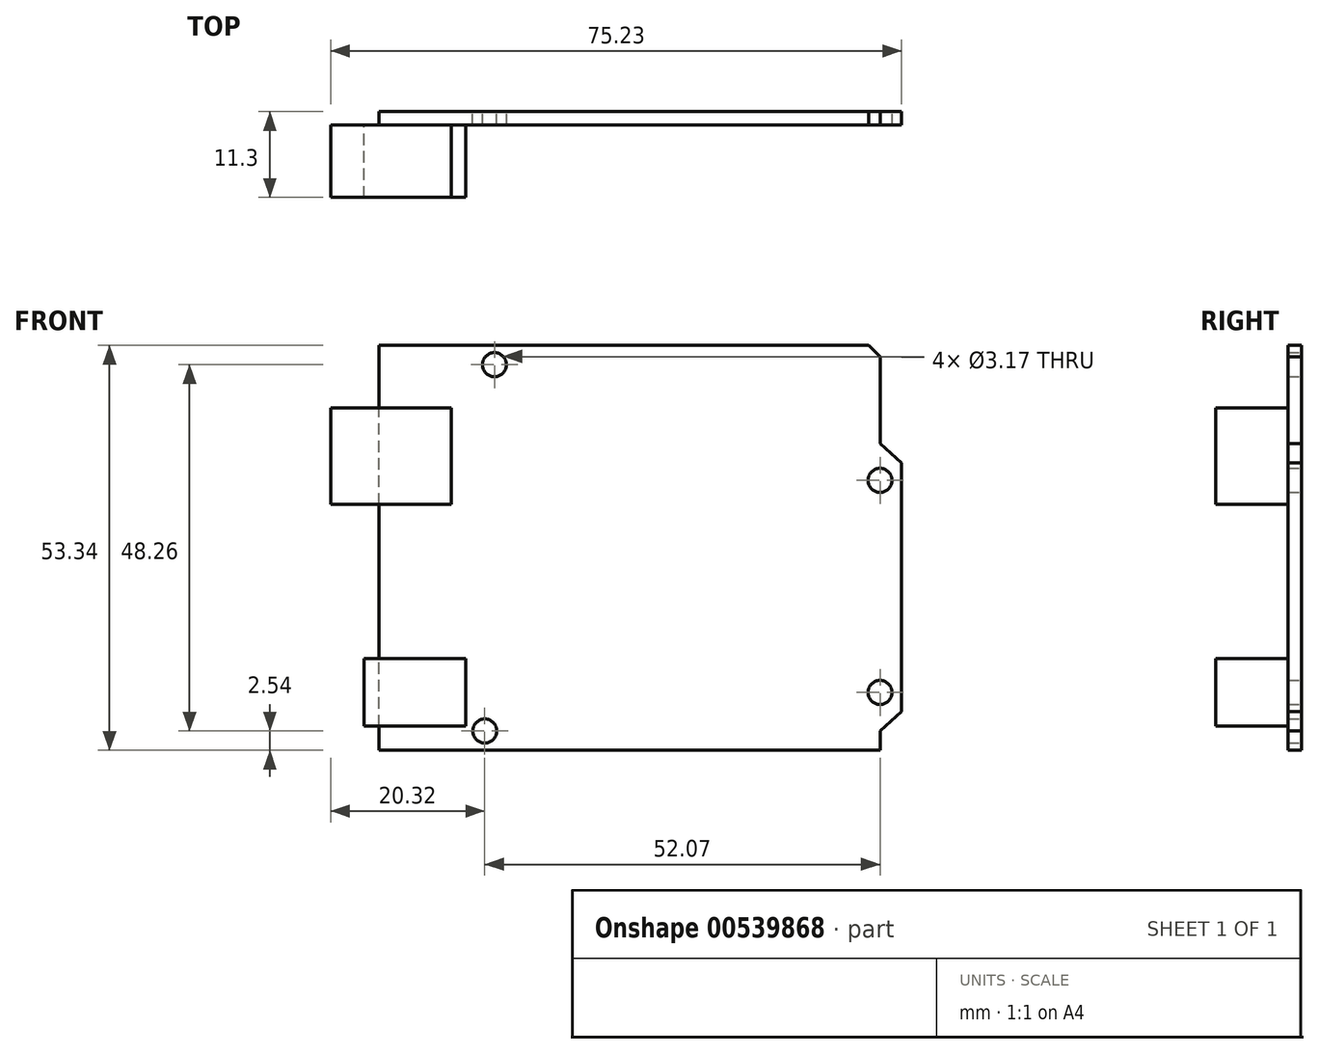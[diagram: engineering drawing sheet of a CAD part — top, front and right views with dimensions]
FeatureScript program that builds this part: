
annotation { "Feature Type Name" : "Feature", "Feature Type Description" : "" }
export const myFeature = defineFeature(function(context is Context, id is Id, definition is map)
    precondition{}
    {
        {
            var Q0;
            Q0=qCreatedBy(makeId("Front.planeOp"),FACE);
            var sketch = newSketch(context, id + "F0", { "sketchPlane" : qUnion([Q0])});
            skLineSegment(sketch, "E0", {"start": v(0, 0) * mm, "end": v(66.04, 0) * mm});
            skLineSegment(sketch, "E1", {"start": v(0, 0) * mm, "end": v(0, 53.34) * mm});
            skLineSegment(sketch, "E2", {"start": v(0, 53.34) * mm, "end": v(64.52, 53.34) * mm});
            skLineSegment(sketch, "E3", {"start": v(66.04, 0) * mm, "end": v(66.04, 2.54) * mm});
            skLineSegment(sketch, "E4", {"start": v(66.04, 2.54) * mm, "end": v(68.88, 5.08) * mm});
            skLineSegment(sketch, "E5", {"start": v(68.88, 37.85) * mm, "end": v(68.88, 5.08) * mm});
            skPoint(sketch, "E6.start.orphan", {"position": v(66.04, 40.39) * mm});
            skLineSegment(sketch, "E7", {"start": v(66.04, 40.39) * mm, "end": v(68.88, 37.85) * mm});
            skLineSegment(sketch, "E8", {"start": v(64.52, 53.34) * mm, "end": v(66.04, 51.82) * mm});
            skLineSegment(sketch, "E9", {"start": v(66.04, 51.82) * mm, "end": v(66.04, 40.39) * mm});
            skCircle(sketch, "E10", {"center": v(15.24, 50.8) * mm, "radius": 1.59 * mm});
            skCircle(sketch, "E11", {"center": v(13.97, 2.54) * mm, "radius": 1.59 * mm});
            skCircle(sketch, "E12", {"center": v(66.04, 35.56) * mm, "radius": 1.59 * mm});
            skCircle(sketch, "E13", {"center": v(66.04, 7.62) * mm, "radius": 1.59 * mm});
            skSolve(sketch);
        }
        {
            var Q0;
            Q0 = qSketchRegion(id + "F0", true);
            extrude(context, id + "F1", {"entities" : qUnion([Q0]), "depth" : 1.78 * mm, "offsetDistance" : 25.4 * mm});
        }
        {
            var Q0;
            Q0=makeQuery(id+"F1.opExtrude","CAP_FACE",FACE,{"disambiguationData":[OSD([sQuery(id+"F0.wireOp",EDGE,"E0"),sQuery(id+"F0.wireOp",EDGE,"E1"),sQuery(id+"F0.wireOp",EDGE,"E2"),sQuery(id+"F0.wireOp",EDGE,"E3"),sQuery(id+"F0.wireOp",EDGE,"E4"),sQuery(id+"F0.wireOp",EDGE,"E5"),sQuery(id+"F0.wireOp",EDGE,"E7"),sQuery(id+"F0.wireOp",EDGE,"E8"),sQuery(id+"F0.wireOp",EDGE,"E9"),sQuery(id+"F0.wireOp",EDGE,"E10"),sQuery(id+"F0.wireOp",EDGE,"E11"),sQuery(id+"F0.wireOp",EDGE,"E12"),sQuery(id+"F0.wireOp",EDGE,"E13")])],"isStart":false});
            var sketch = newSketch(context, id + "F2", { "sketchPlane" : qUnion([Q0])});
            skLineSegment(sketch, "E14.bottom", {"start": v(-6.35, 45.09) * mm, "end": v(9.53, 45.09) * mm});
            skLineSegment(sketch, "E14.top", {"start": v(-6.35, 32.39) * mm, "end": v(9.53, 32.39) * mm});
            skLineSegment(sketch, "E14.left", {"start": v(-6.35, 45.09) * mm, "end": v(-6.35, 32.39) * mm});
            skLineSegment(sketch, "E14.right", {"start": v(9.53, 45.09) * mm, "end": v(9.53, 32.39) * mm});
            skLineSegment(sketch, "E15.bottom", {"start": v(-1.9, 12.07) * mm, "end": v(11.43, 12.07) * mm});
            skLineSegment(sketch, "E15.top", {"start": v(-1.9, 3.18) * mm, "end": v(11.43, 3.18) * mm});
            skLineSegment(sketch, "E15.left", {"start": v(-1.9, 12.06) * mm, "end": v(-1.9, 3.18) * mm});
            skLineSegment(sketch, "E15.right", {"start": v(11.43, 12.06) * mm, "end": v(11.43, 3.18) * mm});
            skPoint(sketch, "E16", {"position": v(0, 32.39) * mm});
            skPoint(sketch, "E17", {"position": v(0, 3.18) * mm});
            skPoint(sketch, "E18", {"position": v(-65.03, 49.69) * mm});
            skSolve(sketch);
        }
        {
            var Q0;
            Q0 = qSketchRegion(id + "F2", true);
            extrude(context, id + "F3", {"entities" : qUnion([Q0]), "depth" : 9.52 * mm, "offsetDistance" : 25.4 * mm});
        }
    });
